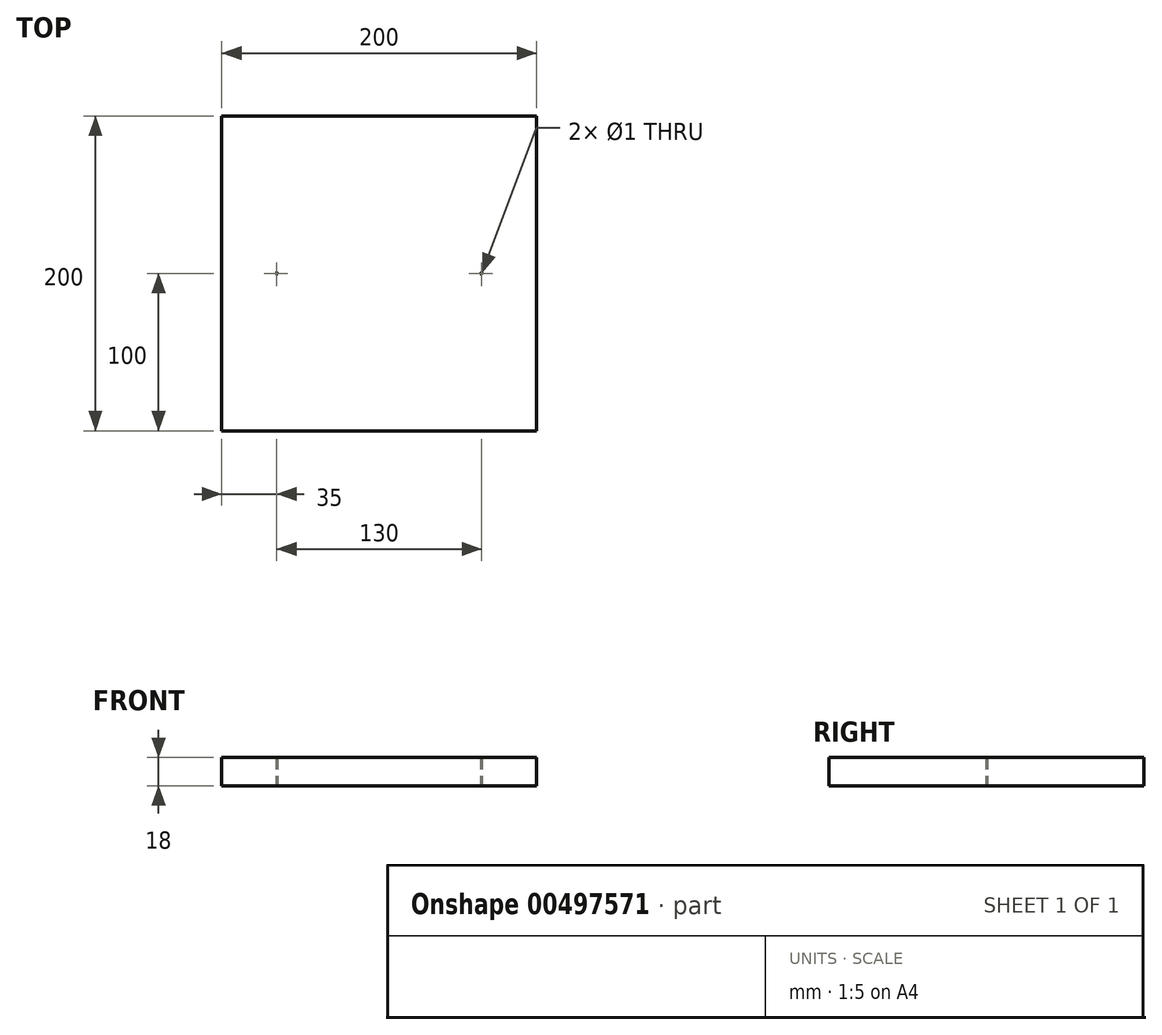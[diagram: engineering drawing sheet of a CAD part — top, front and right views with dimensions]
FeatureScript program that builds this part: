
annotation { "Feature Type Name" : "Feature", "Feature Type Description" : "" }
export const myFeature = defineFeature(function(context is Context, id is Id, definition is map)
    precondition{}
    {
        {
            var Q0;
            Q0=qCreatedBy(makeId("Top.planeOp"),FACE);
            var sketch = newSketch(context, id + "F0", { "sketchPlane" : qUnion([Q0])});
            skLineSegment(sketch, "E0.bottom", {"start": v(0, 0) * mm, "end": v(200, 0) * mm});
            skLineSegment(sketch, "E0.top", {"start": v(0, 200) * mm, "end": v(200, 200) * mm});
            skLineSegment(sketch, "E0.left", {"start": v(0, 0) * mm, "end": v(0, 200) * mm});
            skLineSegment(sketch, "E0.right", {"start": v(200, 0) * mm, "end": v(200, 200) * mm});
            skCircle(sketch, "E1", {"center": v(35, 100) * mm, "radius": 0.5 * mm});
            skLineSegment(sketch, "E2", {"start": v(100, 0) * mm, "end": v(100, 200) * mm, "construction": true});
            skCircle(sketch, "E3.MirrorC", {"center": v(165, 100) * mm, "radius": 0.5 * mm});
            skSolve(sketch);
        }
        {
            var Q0;
            Q0=makeQuery(id+"F0.imprint","IMPRINT",FACE,{"disambiguationData":[TD([[makeQuery(id+"F0.imprint","IMPRINT",EDGE,{"derivedFrom":sQuery(id+"F0.wireOp",EDGE,"E0.bottom")}),1.0]])]});
            extrude(context, id + "F1", {"entities" : qUnion([Q0]), "depth" : 18 * mm});
        }
    });
